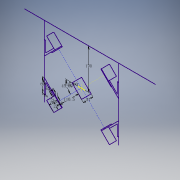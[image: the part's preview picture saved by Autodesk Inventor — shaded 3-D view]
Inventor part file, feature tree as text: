
AUTODESK INVENTOR PART (.ipt)
format: ipt  version: 2016 (Build 200138000, 138)  size: 120,832 bytes
history: native  units: mm
features: sketch x1
ambient origin geometry x8: Origin, YZ Plane, XZ Plane, XY Plane, X Axis, Y Axis, Z Axis, Center Point
feature tree (1):
  sketch  "草图1"  dims[d0=45.0deg d1=57.0mm d2=110.5mm d3=45.0deg d4=21.0mm d5=21.0mm d6=48.0mm d7=3.0mm d8=41.0mm d25=62.0mm d26=60.0mm d27=6.0mm d28=6.0mm d29=170.0mm]
